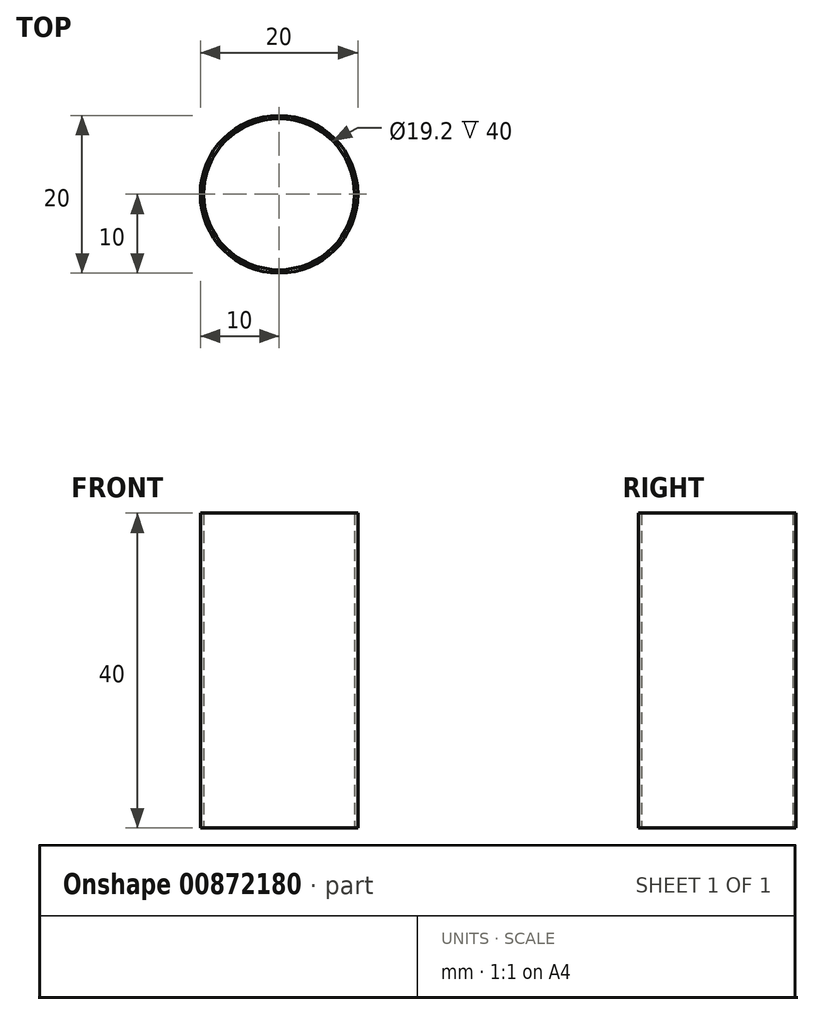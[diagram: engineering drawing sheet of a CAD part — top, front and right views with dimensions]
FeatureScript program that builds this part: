
annotation { "Feature Type Name" : "Feature", "Feature Type Description" : "" }
export const myFeature = defineFeature(function(context is Context, id is Id, definition is map)
    precondition{}
    {
        {
            var Q0;
            Q0=qCreatedBy(makeId("Top.planeOp"),FACE);
            var sketch = newSketch(context, id + "F0", { "sketchPlane" : qUnion([Q0])});
            skCircle(sketch, "E0", {"center": v(0, 0) * mm, "radius": 10 * mm});
            skCircle(sketch, "E1.0", {"center": v(0, 0) * mm, "radius": 9.6 * mm});
            skSolve(sketch);
        }
        {
            var Q0;
            Q0=makeQuery(id+"F0.imprint","IMPRINT",FACE,{"disambiguationData":[TD([[makeQuery(id+"F0.imprint","IMPRINT",EDGE,{"derivedFrom":sQuery(id+"F0.wireOp",EDGE,"E0")}),1.0]])]});
            extrude(context, id + "F1", {"entities" : qUnion([Q0]), "depth" : 40 * mm, "offsetDistance" : 25.4 * mm});
        }
    });
